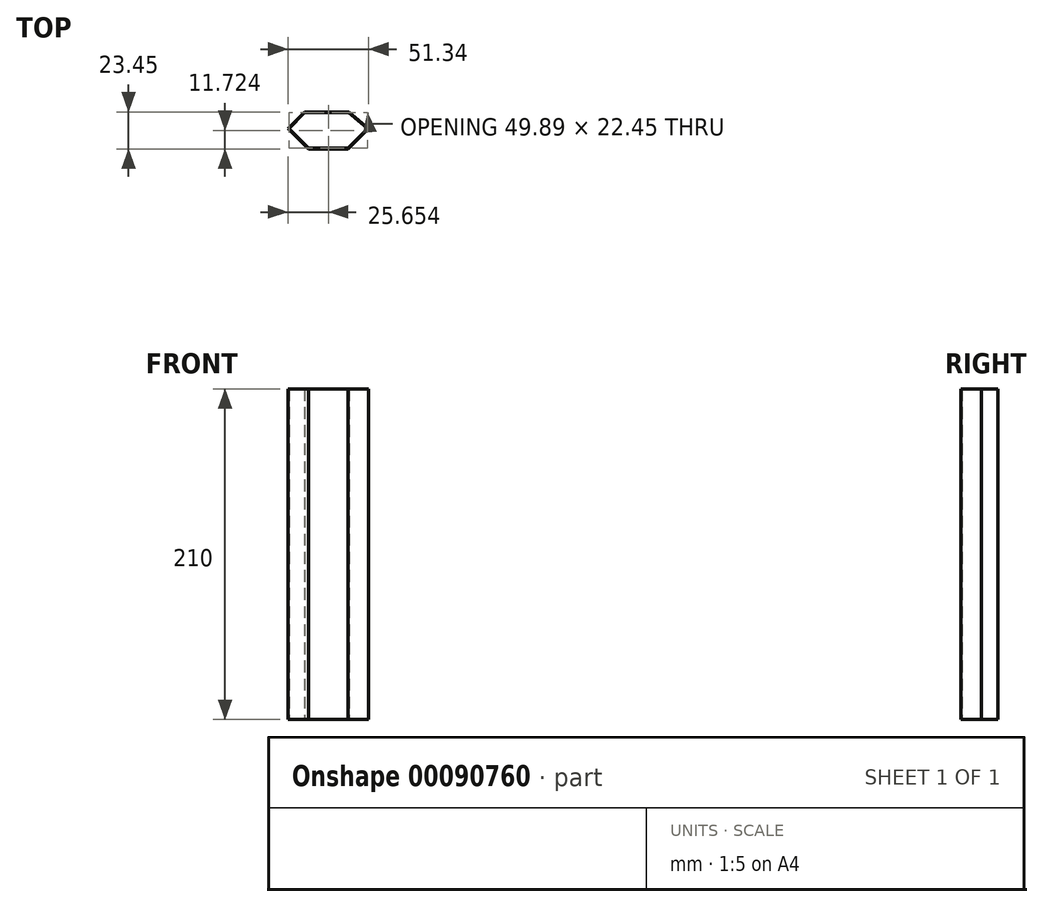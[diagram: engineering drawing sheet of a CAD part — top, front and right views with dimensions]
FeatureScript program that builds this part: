
annotation { "Feature Type Name" : "Feature", "Feature Type Description" : "" }
export const myFeature = defineFeature(function(context is Context, id is Id, definition is map)
    precondition{}
    {
        {
            var Q0;
            Q0=qCreatedBy(makeId("Top.planeOp"),FACE);
            var sketch = newSketch(context, id + "F0", { "sketchPlane" : qUnion([Q0])});
            skCircle(sketch, "E0.0", {"center": v(-78.73, -13.11) * mm, "radius": 1 * mm});
            skCircle(sketch, "E0.1", {"center": v(-67.84, -9.22) * mm, "radius": 2 * mm});
            skCircle(sketch, "E0.2", {"center": v(-46.51, -2.12) * mm, "radius": 2.01 * mm});
            skCircle(sketch, "E0.3", {"center": v(-77.4, -2.12) * mm, "radius": 9.48 * mm});
            skCircle(sketch, "E0.4", {"center": v(-58.3, -2.12) * mm, "radius": 9.48 * mm});
            skLineSegment(sketch, "E0.5", {"start": v(-42.9, -2.12) * mm, "end": v(-92.78, -2.12) * mm});
            skLineSegment(sketch, "E0.6", {"start": v(-92.78, -2.12) * mm, "end": v(-82.8, 7.86) * mm});
            skLineSegment(sketch, "E0.7", {"start": v(-82.8, 7.86) * mm, "end": v(-54.88, 7.86) * mm});
            skLineSegment(sketch, "E0.8", {"start": v(-54.88, 7.86) * mm, "end": v(-42.9, -2.12) * mm});
            skCircle(sketch, "E0.9", {"center": v(-56.44, -13.03) * mm, "radius": 1 * mm});
            skCircle(sketch, "E0.10", {"center": v(-74.1, -12.85) * mm, "radius": 1 * mm});
            skCircle(sketch, "E0.11", {"center": v(-61.16, -12.94) * mm, "radius": 1 * mm});
            skCircle(sketch, "E0.12", {"center": v(-67.84, 5.19) * mm, "radius": 2 * mm});
            skLineSegment(sketch, "E0.13", {"start": v(-80.3, -14.6) * mm, "end": v(-55.36, -14.6) * mm});
            skCircle(sketch, "E0.14", {"center": v(-89.2, -2.12) * mm, "radius": 2.02 * mm});
            skCircle(sketch, "E0.15", {"center": v(-67.84, 5.19) * mm, "radius": 2 * mm});
            skCircle(sketch, "E0.16", {"center": v(-67.84, -9.22) * mm, "radius": 2 * mm});
            skCircle(sketch, "E0.17", {"center": v(-46.51, -2.12) * mm, "radius": 2.01 * mm});
            skCircle(sketch, "E0.18", {"center": v(-89.2, -2.12) * mm, "radius": 2.02 * mm});
            skCircle(sketch, "E0.19", {"center": v(-56.44, -13.03) * mm, "radius": 1 * mm});
            skCircle(sketch, "E0.20", {"center": v(-78.73, -13.11) * mm, "radius": 1 * mm});
            skCircle(sketch, "E0.21", {"center": v(-74.1, -12.85) * mm, "radius": 1 * mm});
            skCircle(sketch, "E0.22", {"center": v(-61.16, -12.94) * mm, "radius": 1 * mm});
            skCircle(sketch, "E0.23", {"center": v(-67.84, 5.19) * mm, "radius": 2 * mm});
            skCircle(sketch, "E0.24", {"center": v(-67.84, -9.22) * mm, "radius": 2 * mm});
            skCircle(sketch, "E0.25", {"center": v(-46.51, -2.12) * mm, "radius": 2.01 * mm});
            skCircle(sketch, "E0.26", {"center": v(-89.2, -2.12) * mm, "radius": 2.02 * mm});
            skCircle(sketch, "E0.27", {"center": v(-56.44, -13.03) * mm, "radius": 1 * mm});
            skCircle(sketch, "E0.28", {"center": v(-78.73, -13.11) * mm, "radius": 1 * mm});
            skCircle(sketch, "E0.29", {"center": v(-74.1, -12.85) * mm, "radius": 1 * mm});
            skCircle(sketch, "E0.30", {"center": v(-61.16, -12.94) * mm, "radius": 1 * mm});
            skLineSegment(sketch, "E1", {"start": v(-42.9, -2.12) * mm, "end": v(-55.36, -14.6) * mm});
            skLineSegment(sketch, "E2", {"start": v(-80.3, -14.6) * mm, "end": v(-92.78, -2.12) * mm});
            skLineSegment(sketch, "E3", {"start": v(-55.36, -14.6) * mm, "end": v(-67.8, -27.06) * mm});
            skLineSegment(sketch, "E4", {"start": v(-67.8, -27.06) * mm, "end": v(-80.3, -14.6) * mm});
            skLineSegment(sketch, "E5.0", {"start": v(-80.52, -15.1) * mm, "end": v(-93.49, -2.12) * mm});
            skLineSegment(sketch, "E5.1", {"start": v(-83.01, 8.36) * mm, "end": v(-54.7, 8.36) * mm});
            skLineSegment(sketch, "E5.2", {"start": v(-54.7, 8.36) * mm, "end": v(-42.15, -2.08) * mm});
            skLineSegment(sketch, "E5.3", {"start": v(-93.49, -2.12) * mm, "end": v(-83.01, 8.36) * mm});
            skLineSegment(sketch, "E5.4", {"start": v(-42.15, -2.08) * mm, "end": v(-55.16, -15.1) * mm});
            skLineSegment(sketch, "E5.5", {"start": v(-80.52, -15.1) * mm, "end": v(-55.16, -15.1) * mm});
            skSolve(sketch);
        }
        {
            var Q0;
            Q0=makeQuery(id+"F0.imprint","IMPRINT",FACE,{"disambiguationData":[TD([[makeQuery(id+"F0.imprint","IMPRINT",EDGE,{"derivedFrom":sQuery(id+"F0.wireOp",EDGE,"E0.6")}),1.0]])]});
            var Q1;
            {var subQ0=sQuery(id+"F0.wireOp",EDGE,"E0.13");Q1=makeQuery(id+"F0.imprint","IMPRINT",FACE,{"disambiguationData":[TD([[makeQuery(id+"F0.imprint","IMPRINT",EDGE,{"derivedFrom":subQ0}),-1.0]])]});}
            extrude(context, id + "F1", {"entities" : qUnion([Q0, Q1]), "depth" : 210 * mm});
        }
    });
